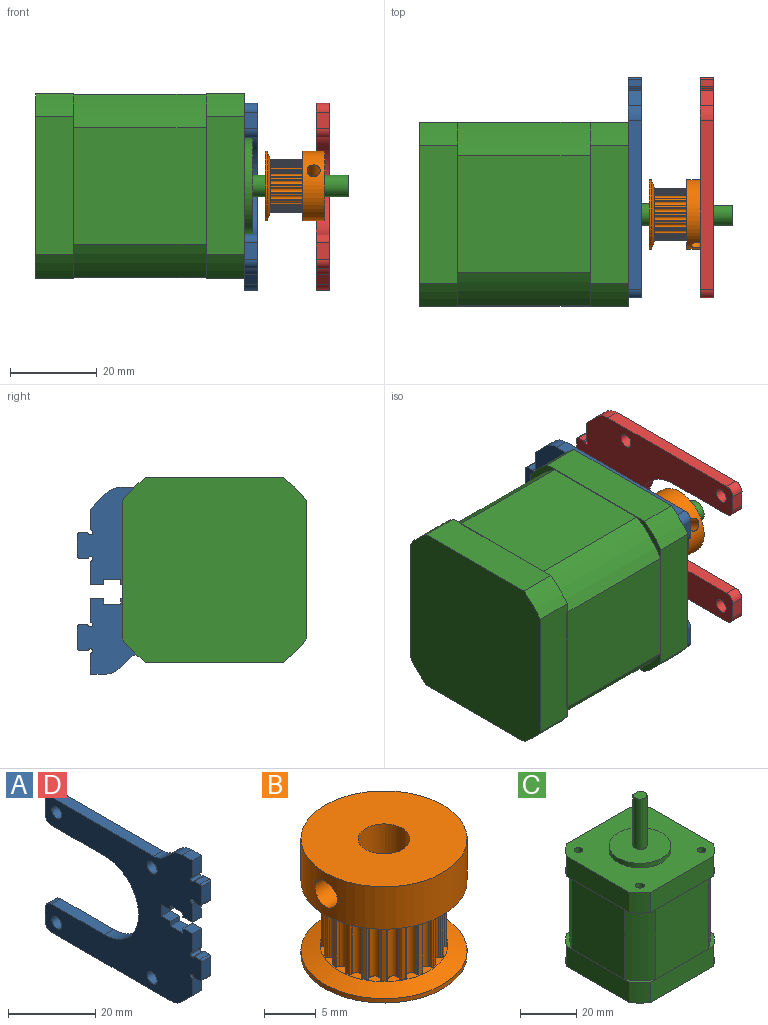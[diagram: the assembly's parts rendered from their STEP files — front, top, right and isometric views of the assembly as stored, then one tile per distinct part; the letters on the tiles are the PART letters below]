
ASSEMBLY  parts=4 mates=3
PART A: 60 faces, bbox 3x50.7x43 mm
  f0: plane 3x1.63mm, normal (0,0,1), area 4.9mm2, adj f1,f54,f58,f59
  f1: cylinder r=0.5mm len=3mm, axis (-1,0,0), area 2.4mm2, adj f0,f2,f58,f59
  f2: plane 5x3mm, normal (0,-1,0), area 15mm2, adj f1,f3,f58,f59
  f3: cylinder r=0.5mm len=3mm, axis (-1,0,0), area 2.4mm2, adj f2,f4,f58,f59
  f4: plane 3x1.63mm, normal (0,0,-1), area 4.9mm2, adj f3,f5,f58,f59
  f5: cylinder r=0.5mm len=3mm, axis (-1,0,0), area 1.6mm2, adj f4,f6,f58,f59
  f6: cylinder r=0.5mm len=3mm, axis (-1,0,0), area 5.5mm2, adj f5,f7,f58,f59
  f7: cylinder r=0.5mm len=3mm, axis (-1,0,0), area 1.6mm2, adj f6,f8,f58,f59
  f8: plane 4.53x3mm, normal (0,-1,0), area 13.6mm2, adj f7,f9,f58,f59
  f9: plane 3.53x3.51mm, normal (0,-0.71,-0.71), area 14.9mm2, adj f8,f10,f58,f59
  f10: cylinder r=5mm len=3.54mm, axis (-1,0,0), area 11.8mm2, adj f9,f11,f58,f59
  f11: plane 38.66x3mm, normal (0,0,-1), area 116mm2, adj f10,f12,f58,f59
  f12: cylinder r=2mm len=3mm, axis (-1,0,0), area 9.4mm2, adj f11,f13,f58,f59
  f13: plane 3.9x3mm, normal (0,1,0), area 11.7mm2, adj f12,f14,f58,f59
  f14: cylinder r=2mm len=3mm, axis (-1,0,0), area 9.4mm2, adj f13,f15,f58,f59
  f15: plane 17.22x3mm, normal (0,0,1), area 51.6mm2, adj f14,f16,f58,f59
  f16: cylinder r=11.1mm len=22.2mm, axis (-1,0,0), area 104.6mm2, adj f15,f17,f58,f59
  f17: plane 17.22x3mm, normal (0,0,-1), area 51.6mm2, adj f16,f18,f58,f59
  f18: cylinder r=2mm len=3mm, axis (-1,0,0), area 9.4mm2, adj f17,f19,f58,f59
  f19: plane 3.9x3mm, normal (0,1,0), area 11.7mm2, adj f18,f20,f58,f59
  f20: cylinder r=2mm len=3mm, axis (-1,0,0), area 9.4mm2, adj f19,f21,f58,f59
  f21: plane 33.22x3mm, normal (0,0,1), area 99.7mm2, adj f20,f22,f58,f59
  f22: cylinder r=5mm len=3.43mm, axis (-1,0,0), area 11.3mm2, adj f21,f23,f58,f59
  f23: plane 3x2.42mm, normal (0,0.69,0.73), area 10mm2, adj f22,f24,f58,f59
  f24: cylinder r=5mm len=3.43mm, axis (-1,0,0), area 11.3mm2, adj f23,f25,f58,f59
  f25: plane 3.22x3mm, normal (0,0,1), area 9.7mm2, adj f24,f26,f58,f59
  f26: plane 4.53x3mm, normal (0,-1,0), area 13.6mm2, adj f25,f27,f58,f59
  f27: cylinder r=0.5mm len=3mm, axis (-1,0,0), area 1.6mm2, adj f26,f28,f58,f59
  f28: cylinder r=0.5mm len=3mm, axis (-1,0,0), area 5.5mm2, adj f27,f29,f58,f59
  f29: cylinder r=0.5mm len=3mm, axis (-1,0,0), area 1.6mm2, adj f28,f30,f58,f59
  f30: plane 3x1.63mm, normal (0,0,1), area 4.9mm2, adj f29,f31,f58,f59
  f31: cylinder r=0.5mm len=3mm, axis (-1,0,0), area 2.4mm2, adj f30,f32,f58,f59
  f32: plane 5x3mm, normal (0,-1,0), area 15mm2, adj f31,f33,f58,f59
  f33: cylinder r=0.5mm len=3mm, axis (-1,0,0), area 2.4mm2, adj f32,f34,f58,f59
  f34: plane 3x1.63mm, normal (0,0,-1), area 4.9mm2, adj f33,f35,f58,f59
  f35: cylinder r=0.5mm len=3mm, axis (-1,0,0), area 1.6mm2, adj f34,f36,f58,f59
  f36: cylinder r=0.5mm len=3mm, axis (-1,0,0), area 5.5mm2, adj f35,f37,f58,f59
  f37: cylinder r=0.5mm len=3mm, axis (-1,0,0), area 1.6mm2, adj f36,f38,f58,f59
  f38: plane 5.13x3mm, normal (0,-1,0), area 15.4mm2, adj f37,f39,f58,f59
  f39: plane 3x3mm, normal (0,0,-1), area 9mm2, adj f38,f40,f58,f59
  f40: plane 3x1.28mm, normal (0,1,0), area 3.8mm2, adj f39,f41,f58,f59
  f41: plane 4x3mm, normal (0,0,-1), area 12mm2, adj f40,f42,f58,f59
  f42: plane 3x1.28mm, normal (0,-1,0), area 3.8mm2, adj f41,f43,f58,f59
  f43: plane 3x3mm, normal (0,0,-1), area 9mm2, adj f42,f44,f58,f59
  f44: plane 3.2x3mm, normal (0,-1,0), area 9.6mm2, adj f43,f45,f58,f59
  f45: plane 3x3mm, normal (0,0,1), area 9mm2, adj f44,f46,f58,f59
  f46: plane 3x1.28mm, normal (0,-1,0), area 3.8mm2, adj f45,f47,f58,f59
  f47: plane 4x3mm, normal (0,0,1), area 12mm2, adj f46,f48,f58,f59
  f48: plane 3x1.28mm, normal (0,1,0), area 3.8mm2, adj f47,f49,f58,f59
  f49: plane 3x3mm, normal (0,0,1), area 9mm2, adj f48,f50,f58,f59
  f50: plane 5.13x3mm, normal (0,-1,0), area 15.4mm2, adj f49,f51,f58,f59
  f51: cylinder r=0.5mm len=3mm, axis (-1,0,0), area 1.6mm2, adj f50,f52,f58,f59
  f52: cylinder r=0.5mm len=3mm, axis (-1,0,0), area 5.5mm2, adj f51,f54,f58,f59
  f53: cylinder r=1.6mm len=3.2mm, axis (-1,0,0), area 30.2mm2, adj f58,f59
  f54: cylinder r=0.5mm len=3mm, axis (-1,0,0), area 1.6mm2, adj f0,f52,f58,f59
  f55: cylinder r=1.6mm len=3.2mm, axis (-1,0,0), area 30.2mm2, adj f58,f59
  f56: cylinder r=1.6mm len=3.2mm, axis (-1,0,0), area 30.2mm2, adj f58,f59
  f57: cylinder r=1.6mm len=3.2mm, axis (-1,0,0), area 30.2mm2, adj f58,f59
  f58: plane 50.72x43mm, normal (1,0,0), area 1174.8mm2, adj f0,f1,f2,f3,f4,f5,f6,f7
  f59: plane 50.72x43mm, normal (-1,0,0), area 1174.8mm2, adj f0,f1,f2,f3,f4,f5,f6,f7
PART B: 131 faces, bbox 16x16x13.7 mm
  f0: plane 6.35x6.35mm, normal (0,0,-1), area 12mm2, adj f125,f127
  f1: cylinder r=1.5mm len=6mm, axis (1,0,0), area 53.5mm2, adj f123,f125
  f2: cylinder r=1mm len=7.5mm, axis (0,0,-1), area 1.9mm2, adj f3,f121,f122,f126
  f3: cylinder r=0.15mm len=7.5mm, axis (0,0,-1), area 1.4mm2, adj f2,f4,f122,f126
  f4: cylinder r=6mm len=7.5mm, axis (0,0,-1), area 3.3mm2, adj f3,f5,f122,f126
  f5: cylinder r=0.15mm len=7.5mm, axis (0,0,-1), area 1.4mm2, adj f4,f6,f122,f126
  f6: cylinder r=1mm len=7.5mm, axis (0,0,-1), area 1.9mm2, adj f5,f7,f122,f126
  f7: cylinder r=0.56mm len=7.5mm, axis (0,0,-1), area 9.8mm2, adj f6,f8,f122,f126
  f8: cylinder r=1mm len=7.5mm, axis (0,0,-1), area 1.9mm2, adj f7,f9,f122,f126
  f9: cylinder r=0.15mm len=7.5mm, axis (0,0,-1), area 1.4mm2, adj f8,f10,f122,f126
  f10: cylinder r=6mm len=7.5mm, axis (0,0,-1), area 3.3mm2, adj f9,f11,f122,f126
  f11: cylinder r=0.15mm len=7.5mm, axis (0,0,-1), area 1.4mm2, adj f10,f12,f122,f126
  f12: cylinder r=1mm len=7.5mm, axis (0,0,-1), area 1.9mm2, adj f11,f13,f122,f126
  f13: cylinder r=0.56mm len=7.5mm, axis (0,0,-1), area 9.8mm2, adj f12,f14,f122,f126
  f14: cylinder r=1mm len=7.5mm, axis (0,0,-1), area 1.9mm2, adj f13,f15,f122,f126
  f15: cylinder r=0.15mm len=7.5mm, axis (0,0,-1), area 1.4mm2, adj f14,f16,f122,f126
  f16: cylinder r=6mm len=7.5mm, axis (0,0,-1), area 3.3mm2, adj f15,f17,f122,f126
  f17: cylinder r=0.15mm len=7.5mm, axis (0,0,-1), area 1.4mm2, adj f16,f18,f122,f126
  f18: cylinder r=1mm len=7.5mm, axis (0,0,-1), area 1.9mm2, adj f17,f19,f122,f126
  f19: cylinder r=0.56mm len=7.5mm, axis (0,0,-1), area 9.8mm2, adj f18,f20,f122,f126
  f20: cylinder r=1mm len=7.5mm, axis (0,0,-1), area 1.9mm2, adj f19,f21,f122,f126
  f21: cylinder r=0.15mm len=7.5mm, axis (0,0,-1), area 1.4mm2, adj f20,f22,f122,f126
  f22: cylinder r=6mm len=7.5mm, axis (0,0,-1), area 3.3mm2, adj f21,f23,f122,f126
  f23: cylinder r=0.15mm len=7.5mm, axis (0,0,-1), area 1.4mm2, adj f22,f24,f122,f126
  f24: cylinder r=1mm len=7.5mm, axis (0,0,-1), area 1.9mm2, adj f23,f25,f122,f126
  f25: cylinder r=0.56mm len=7.5mm, axis (0,0,-1), area 9.8mm2, adj f24,f26,f122,f126
  f26: cylinder r=1mm len=7.5mm, axis (0,0,-1), area 1.9mm2, adj f25,f27,f122,f126
  f27: cylinder r=0.15mm len=7.5mm, axis (0,0,-1), area 1.4mm2, adj f26,f28,f122,f126
  f28: cylinder r=6mm len=7.5mm, axis (0,0,-1), area 2.8mm2, adj f27,f29,f122,f126
  f29: cylinder r=0.15mm len=7.5mm, axis (0,0,-1), area 2mm2, adj f28,f30,f122,f126
  f30: cylinder r=1mm len=7.5mm, axis (0,0,-1), area 1.9mm2, adj f29,f31,f122,f126
  f31: cylinder r=0.56mm len=7.5mm, axis (0,0,-1), area 9.8mm2, adj f30,f32,f122,f126
  f32: cylinder r=1mm len=7.5mm, axis (0,0,-1), area 1.9mm2, adj f31,f33,f122,f126
  f33: cylinder r=0.15mm len=7.5mm, axis (0,0,-1), area 1.4mm2, adj f32,f34,f122,f126
  f34: cylinder r=6mm len=7.5mm, axis (0,0,-1), area 3.3mm2, adj f33,f35,f122,f126
  f35: cylinder r=0.15mm len=7.5mm, axis (0,0,-1), area 1.4mm2, adj f34,f36,f122,f126
  f36: cylinder r=1mm len=7.5mm, axis (0,0,-1), area 1.9mm2, adj f35,f37,f122,f126
  f37: cylinder r=0.56mm len=7.5mm, axis (0,0,-1), area 9.8mm2, adj f36,f38,f122,f126
  f38: cylinder r=1mm len=7.5mm, axis (0,0,-1), area 1.9mm2, adj f37,f39,f122,f126
  f39: cylinder r=0.15mm len=7.5mm, axis (0,0,-1), area 1.4mm2, adj f38,f40,f122,f126
  f40: cylinder r=6mm len=7.5mm, axis (0,0,-1), area 3.3mm2, adj f39,f41,f122,f126
  f41: cylinder r=0.15mm len=7.5mm, axis (0,0,-1), area 1.4mm2, adj f40,f42,f122,f126
  f42: cylinder r=1mm len=7.5mm, axis (0,0,-1), area 1.9mm2, adj f41,f43,f122,f126
  f43: cylinder r=0.56mm len=7.5mm, axis (0,0,-1), area 9.8mm2, adj f42,f44,f122,f126
  f44: cylinder r=1mm len=7.5mm, axis (0,0,-1), area 1.9mm2, adj f43,f45,f122,f126
  f45: cylinder r=0.15mm len=7.5mm, axis (0,0,-1), area 1.4mm2, adj f44,f46,f122,f126
  f46: cylinder r=6mm len=7.5mm, axis (0,0,-1), area 3.3mm2, adj f45,f47,f122,f126
  f47: cylinder r=0.15mm len=7.5mm, axis (0,0,-1), area 1.4mm2, adj f46,f48,f122,f126
  f48: cylinder r=1mm len=7.5mm, axis (0,0,-1), area 1.9mm2, adj f47,f49,f122,f126
  f49: cylinder r=0.56mm len=7.5mm, axis (0,0,-1), area 9.8mm2, adj f48,f50,f122,f126
  f50: cylinder r=1mm len=7.5mm, axis (0,0,-1), area 1.9mm2, adj f49,f51,f122,f126
  f51: cylinder r=0.15mm len=7.5mm, axis (0,0,-1), area 1.4mm2, adj f50,f52,f122,f126
  f52: cylinder r=6mm len=7.5mm, axis (0,0,-1), area 3.3mm2, adj f51,f53,f122,f126
  f53: cylinder r=0.15mm len=7.5mm, axis (0,0,-1), area 1.4mm2, adj f52,f54,f122,f126
  f54: cylinder r=1mm len=7.5mm, axis (0,0,-1), area 1.9mm2, adj f53,f55,f122,f126
  f55: cylinder r=0.56mm len=7.5mm, axis (0,0,-1), area 9.8mm2, adj f54,f56,f122,f126
  f56: cylinder r=1mm len=7.5mm, axis (0,0,-1), area 1.9mm2, adj f55,f57,f122,f126
  f57: cylinder r=0.15mm len=7.5mm, axis (0,0,-1), area 1.4mm2, adj f56,f58,f122,f126
  f58: cylinder r=6mm len=7.5mm, axis (0,0,-1), area 3.3mm2, adj f57,f59,f122,f126
  f59: cylinder r=0.15mm len=7.5mm, axis (0,0,-1), area 1.4mm2, adj f58,f60,f122,f126
  f60: cylinder r=1mm len=7.5mm, axis (0,0,-1), area 1.9mm2, adj f59,f61,f122,f126
  f61: cylinder r=0.56mm len=7.5mm, axis (0,0,-1), area 9.8mm2, adj f60,f62,f122,f126
  f62: cylinder r=1mm len=7.5mm, axis (0,0,-1), area 1.9mm2, adj f61,f63,f122,f126
  f63: cylinder r=0.15mm len=7.5mm, axis (0,0,-1), area 1.4mm2, adj f62,f64,f122,f126
  f64: cylinder r=6mm len=7.5mm, axis (0,0,-1), area 3.3mm2, adj f63,f65,f122,f126
  f65: cylinder r=0.15mm len=7.5mm, axis (0,0,-1), area 1.4mm2, adj f64,f66,f122,f126
  f66: cylinder r=1mm len=7.5mm, axis (0,0,-1), area 1.9mm2, adj f65,f67,f122,f126
  f67: cylinder r=0.56mm len=7.5mm, axis (0,0,-1), area 9.8mm2, adj f66,f68,f122,f126
  f68: cylinder r=1mm len=7.5mm, axis (0,0,-1), area 1.9mm2, adj f67,f69,f122,f126
  f69: cylinder r=0.15mm len=7.5mm, axis (0,0,-1), area 1.4mm2, adj f68,f70,f122,f126
  f70: cylinder r=6mm len=7.5mm, axis (0,0,-1), area 3.3mm2, adj f69,f71,f122,f126
  f71: cylinder r=0.15mm len=7.5mm, axis (0,0,-1), area 1.4mm2, adj f70,f72,f122,f126
  f72: cylinder r=1mm len=7.5mm, axis (0,0,-1), area 1.9mm2, adj f71,f73,f122,f126
  f73: cylinder r=0.56mm len=7.5mm, axis (0,0,-1), area 9.8mm2, adj f72,f74,f122,f126
  f74: cylinder r=1mm len=7.5mm, axis (0,0,-1), area 1.9mm2, adj f73,f75,f122,f126
  f75: cylinder r=0.15mm len=7.5mm, axis (0,0,-1), area 1.4mm2, adj f74,f76,f122,f126
  f76: cylinder r=6mm len=7.5mm, axis (0,0,-1), area 3.3mm2, adj f75,f77,f122,f126
  f77: cylinder r=0.15mm len=7.5mm, axis (0,0,-1), area 1.4mm2, adj f76,f78,f122,f126
  f78: cylinder r=1mm len=7.5mm, axis (0,0,-1), area 1.9mm2, adj f77,f79,f122,f126
  f79: cylinder r=0.56mm len=7.5mm, axis (0,0,-1), area 9.8mm2, adj f78,f80,f122,f126
  f80: cylinder r=1mm len=7.5mm, axis (0,0,-1), area 1.9mm2, adj f79,f81,f122,f126
  f81: cylinder r=0.15mm len=7.5mm, axis (0,0,-1), area 1.4mm2, adj f80,f82,f122,f126
  f82: cylinder r=6mm len=7.5mm, axis (0,0,-1), area 3.3mm2, adj f81,f83,f122,f126
  f83: cylinder r=0.15mm len=7.5mm, axis (0,0,-1), area 1.4mm2, adj f82,f84,f122,f126
  f84: cylinder r=1mm len=7.5mm, axis (0,0,-1), area 1.9mm2, adj f83,f85,f122,f126
  f85: cylinder r=0.56mm len=7.5mm, axis (0,0,-1), area 9.8mm2, adj f84,f86,f122,f126
  f86: cylinder r=1mm len=7.5mm, axis (0,0,-1), area 1.9mm2, adj f85,f87,f122,f126
  f87: cylinder r=0.15mm len=7.5mm, axis (0,0,-1), area 1.4mm2, adj f86,f88,f122,f126
  f88: cylinder r=6mm len=7.5mm, axis (0,0,-1), area 3.3mm2, adj f87,f89,f122,f126
  f89: cylinder r=0.15mm len=7.5mm, axis (0,0,-1), area 1.4mm2, adj f88,f90,f122,f126
  f90: cylinder r=1mm len=7.5mm, axis (0,0,-1), area 1.9mm2, adj f89,f91,f122,f126
  f91: cylinder r=0.56mm len=7.5mm, axis (0,0,-1), area 9.8mm2, adj f90,f92,f122,f126
  f92: cylinder r=1mm len=7.5mm, axis (0,0,-1), area 1.9mm2, adj f91,f93,f122,f126
  f93: cylinder r=0.15mm len=7.5mm, axis (0,0,-1), area 1.4mm2, adj f92,f94,f122,f126
  f94: cylinder r=6mm len=7.5mm, axis (0,0,-1), area 3.3mm2, adj f93,f95,f122,f126
  f95: cylinder r=0.15mm len=7.5mm, axis (0,0,-1), area 1.4mm2, adj f94,f96,f122,f126
  f96: cylinder r=1mm len=7.5mm, axis (0,0,-1), area 1.9mm2, adj f95,f97,f122,f126
  f97: cylinder r=0.56mm len=7.5mm, axis (0,0,-1), area 9.8mm2, adj f96,f98,f122,f126
  f98: cylinder r=1mm len=7.5mm, axis (0,0,-1), area 1.9mm2, adj f97,f99,f122,f126
  f99: cylinder r=0.15mm len=7.5mm, axis (0,0,-1), area 1.4mm2, adj f98,f100,f122,f126
  f100: cylinder r=6mm len=7.5mm, axis (0,0,-1), area 3.3mm2, adj f99,f101,f122,f126
  f101: cylinder r=0.15mm len=7.5mm, axis (0,0,-1), area 1.4mm2, adj f100,f102,f122,f126
  f102: cylinder r=1mm len=7.5mm, axis (0,0,-1), area 1.9mm2, adj f101,f103,f122,f126
  f103: cylinder r=0.56mm len=7.5mm, axis (0,0,-1), area 9.8mm2, adj f102,f104,f122,f126
  f104: cylinder r=1mm len=7.5mm, axis (0,0,-1), area 1.9mm2, adj f103,f105,f122,f126
  f105: cylinder r=0.15mm len=7.5mm, axis (0,0,-1), area 1.4mm2, adj f104,f106,f122,f126
  f106: cylinder r=6mm len=7.5mm, axis (0,0,-1), area 3.3mm2, adj f105,f107,f122,f126
  f107: cylinder r=0.15mm len=7.5mm, axis (0,0,-1), area 1.4mm2, adj f106,f108,f122,f126
  f108: cylinder r=1mm len=7.5mm, axis (0,0,-1), area 1.9mm2, adj f107,f109,f122,f126
  f109: cylinder r=0.56mm len=7.5mm, axis (0,0,-1), area 9.8mm2, adj f108,f110,f122,f126
  f110: cylinder r=1mm len=7.5mm, axis (0,0,-1), area 1.9mm2, adj f109,f111,f122,f126
  f111: cylinder r=0.15mm len=7.5mm, axis (0,0,-1), area 1.4mm2, adj f110,f112,f122,f126
  f112: cylinder r=6mm len=7.5mm, axis (0,0,-1), area 3.3mm2, adj f111,f113,f122,f126
  f113: cylinder r=0.15mm len=7.5mm, axis (0,0,-1), area 1.4mm2, adj f112,f114,f122,f126
  f114: cylinder r=1mm len=7.5mm, axis (0,0,-1), area 1.9mm2, adj f113,f115,f122,f126
  f115: cylinder r=0.56mm len=7.5mm, axis (0,0,-1), area 9.8mm2, adj f114,f116,f122,f126
  f116: cylinder r=1mm len=7.5mm, axis (0,0,-1), area 1.9mm2, adj f115,f117,f122,f126
  f117: cylinder r=0.15mm len=7.5mm, axis (0,0,-1), area 1.4mm2, adj f116,f118,f122,f126
  f118: cylinder r=6mm len=7.5mm, axis (0,0,-1), area 3.3mm2, adj f117,f119,f122,f126
  f119: cylinder r=0.15mm len=7.5mm, axis (0,0,-1), area 1.4mm2, adj f118,f120,f122,f126
  f120: cylinder r=1mm len=7.5mm, axis (0,0,-1), area 1.9mm2, adj f119,f121,f122,f126
  f121: cylinder r=0.56mm len=7.5mm, axis (0,0,-1), area 9.8mm2, adj f2,f120,f122,f126
  f122: plane 16x16mm, normal (0,0,-1), area 102.3mm2, adj f2,f3,f4,f5,f6,f7,f8,f9
  f123: cylinder r=8mm len=16mm, axis (0,0,-1), area 244.2mm2, adj f1,f122,f124
  f124: plane 16x16mm, normal (0,0,1), area 181.4mm2, adj f123,f125
  f125: cylinder r=2.5mm len=12.5mm, axis (0,0,-1), area 188.9mm2, adj f0,f1,f124
  f126: plane 12.28x12.28mm, normal (0,0,1), area 19.8mm2, adj f2,f3,f4,f5,f6,f7,f8,f9
  f127: cylinder r=3.17mm len=6.35mm, axis (0,0,1), area 23.9mm2, adj f0,f128
  f128: plane 16x16mm, normal (0,0,-1), area 169.4mm2, adj f127,f129
  f129: cylinder r=8mm len=16mm, axis (0,0,1), area 25.5mm2, adj f128,f130
  f130: cone r=6.14mm half-angle=69.6deg, axis (0,0,-1), area 88.1mm2, adj f126,f129
PART C: 50 faces, bbox 42.4x42.4x72 mm
  f0: cylinder r=2.5mm len=22mm, axis (0,0,-1), area 297.3mm2, adj f1,f2,f29,f30
  f1: plane 5x4.5mm, normal (0,0,1), area 18.6mm2, adj f0,f29
  f2: plane 22x22mm, normal (0,0,1), area 360.5mm2, adj f0,f3
  f3: cylinder r=11mm len=22mm, axis (0,0,-1), area 138.2mm2, adj f2,f8
  f4: plane 31.78x8.75mm, normal (1,0,0), area 278mm2, adj f8,f9,f10,f32
  f5: plane 31.78x8.75mm, normal (0,-1,0), area 278mm2, adj f8,f9,f11,f32
  f6: plane 31.78x8.75mm, normal (-1,0,0), area 278mm2, adj f8,f11,f12,f32
  f7: plane 31.78x8.75mm, normal (0,1,0), area 278mm2, adj f8,f10,f12,f32
  f8: plane 42.42x42.42mm, normal (0,0,1), area 1339.6mm2, adj f3,f4,f5,f6,f7,f9,f10,f11
  f9: cylinder r=26.5mm len=8.75mm, axis (0,0,-1), area 66.1mm2, adj f4,f5,f8,f32
  f10: cylinder r=26.5mm len=8.75mm, axis (0,0,-1), area 66.1mm2, adj f4,f7,f8,f32
  f11: cylinder r=26.5mm len=8.75mm, axis (0,0,-1), area 66.1mm2, adj f5,f6,f8,f32
  f12: cylinder r=26.5mm len=8.75mm, axis (0,0,-1), area 66.1mm2, adj f6,f7,f8,f32
  f13: cone r=1.25mm half-angle=59deg, axis (0,0,1), area 5.7mm2, adj f14
  f14: cylinder r=1.25mm len=2.5mm, axis (0,0,1), area 11.8mm2, adj f13,f15
  f15: plane 3x3mm, normal (0,0,1), area 2.2mm2, adj f14,f16
  f16: cylinder r=1.5mm len=6mm, axis (0,0,1), area 56.5mm2, adj f8,f15
  f17: cone r=1.25mm half-angle=59deg, axis (0,0,1), area 5.7mm2, adj f18
  f18: cylinder r=1.25mm len=2.5mm, axis (0,0,1), area 11.8mm2, adj f17,f19
  f19: plane 3x3mm, normal (0,0,1), area 2.2mm2, adj f18,f20
  f20: cylinder r=1.5mm len=6mm, axis (0,0,1), area 56.5mm2, adj f8,f19
  f21: cone r=1.25mm half-angle=59deg, axis (0,0,1), area 5.7mm2, adj f22
  f22: cylinder r=1.25mm len=2.5mm, axis (0,0,1), area 11.8mm2, adj f21,f23
  f23: plane 3x3mm, normal (0,0,1), area 2.2mm2, adj f22,f24
  f24: cylinder r=1.5mm len=6mm, axis (0,0,1), area 56.5mm2, adj f8,f23
  f25: cone r=1.25mm half-angle=59deg, axis (0,0,1), area 5.7mm2, adj f26
  f26: cylinder r=1.25mm len=2.5mm, axis (0,0,1), area 11.8mm2, adj f25,f27
  f27: plane 3x3mm, normal (0,0,1), area 2.2mm2, adj f26,f28
  f28: cylinder r=1.5mm len=6mm, axis (0,0,1), area 56.5mm2, adj f8,f27
  f29: plane 15x3mm, normal (0,1,0), area 45mm2, adj f0,f1,f30
  f30: plane 3x0.5mm, normal (0,0,1), area 1mm2, adj f0,f29
  f31: plane 42.42x42.42mm, normal (0,0,1), area 67.2mm2, adj f33,f34,f35,f36,f37,f38,f39,f40
  f32: plane 42.42x42.42mm, normal (0,0,-1), area 67.2mm2, adj f4,f5,f6,f7,f9,f10,f11,f12
  f33: cylinder r=25mm len=30.5mm, axis (0,0,1), area 335.5mm2, adj f31,f32,f34,f40
  f34: plane 30.5x26.79mm, normal (0,1,0), area 817.1mm2, adj f31,f32,f33,f35
  f35: cylinder r=25mm len=30.5mm, axis (0,0,1), area 335.5mm2, adj f31,f32,f34,f36
  f36: plane 30.5x26.79mm, normal (1,0,0), area 817.1mm2, adj f31,f32,f35,f37
  f37: cylinder r=25mm len=30.5mm, axis (0,0,1), area 335.5mm2, adj f31,f32,f36,f38
  f38: plane 30.5x26.79mm, normal (0,-1,0), area 817.1mm2, adj f31,f32,f37,f39
  f39: cylinder r=25mm len=30.5mm, axis (0,0,1), area 335.5mm2, adj f31,f32,f38,f40
  f40: plane 30.5x26.79mm, normal (-1,0,0), area 817.1mm2, adj f31,f32,f33,f39
  f41: plane 42.42x42.42mm, normal (0,0,-1), area 1748.1mm2, adj f42,f43,f44,f45,f46,f47,f48,f49
  f42: cylinder r=26.5mm len=8.75mm, axis (0,0,-1), area 66.1mm2, adj f31,f41,f48,f49
  f43: cylinder r=26.5mm len=8.75mm, axis (0,0,-1), area 66.1mm2, adj f31,f41,f47,f48
  f44: cylinder r=26.5mm len=8.75mm, axis (0,0,-1), area 66.1mm2, adj f31,f41,f46,f47
  f45: cylinder r=26.5mm len=8.75mm, axis (0,0,-1), area 66.1mm2, adj f31,f41,f46,f49
  f46: plane 31.78x8.75mm, normal (0,1,0), area 278mm2, adj f31,f41,f44,f45
  f47: plane 31.78x8.75mm, normal (-1,0,0), area 278mm2, adj f31,f41,f43,f44
  f48: plane 31.78x8.75mm, normal (0,-1,0), area 278mm2, adj f31,f41,f42,f43
  f49: plane 31.78x8.75mm, normal (1,0,0), area 278mm2, adj f31,f41,f42,f45
PART D: same geometry as A
PLACE A rot(axis=(1,0,0),180deg) t=(-10.18,52.64,17.38)mm fixed
PLACE B rot(axis=(0.47,0.75,0.47),106.2deg) t=(-4.18,27.65,-0.15)mm
PLACE C rot(axis=(0,1,0),90deg) t=(-10.18,27.65,-0.15)mm
PLACE D rot(axis=(1,0,0),180deg) t=(6.42,52.64,17.38)mm
MATE revolute B.f4 <-> C.f0  axis (1,0,0) through (8.32,27.65,-0.15)mm
MATE fastened C.f25 <-> A.f55  axis (1,0,0) through (-10.18,43.15,15.35)mm
MATE fastened D.f50 <-> A.f38  axis (0,1,0) through (7.92,56.15,-5.15)mm
